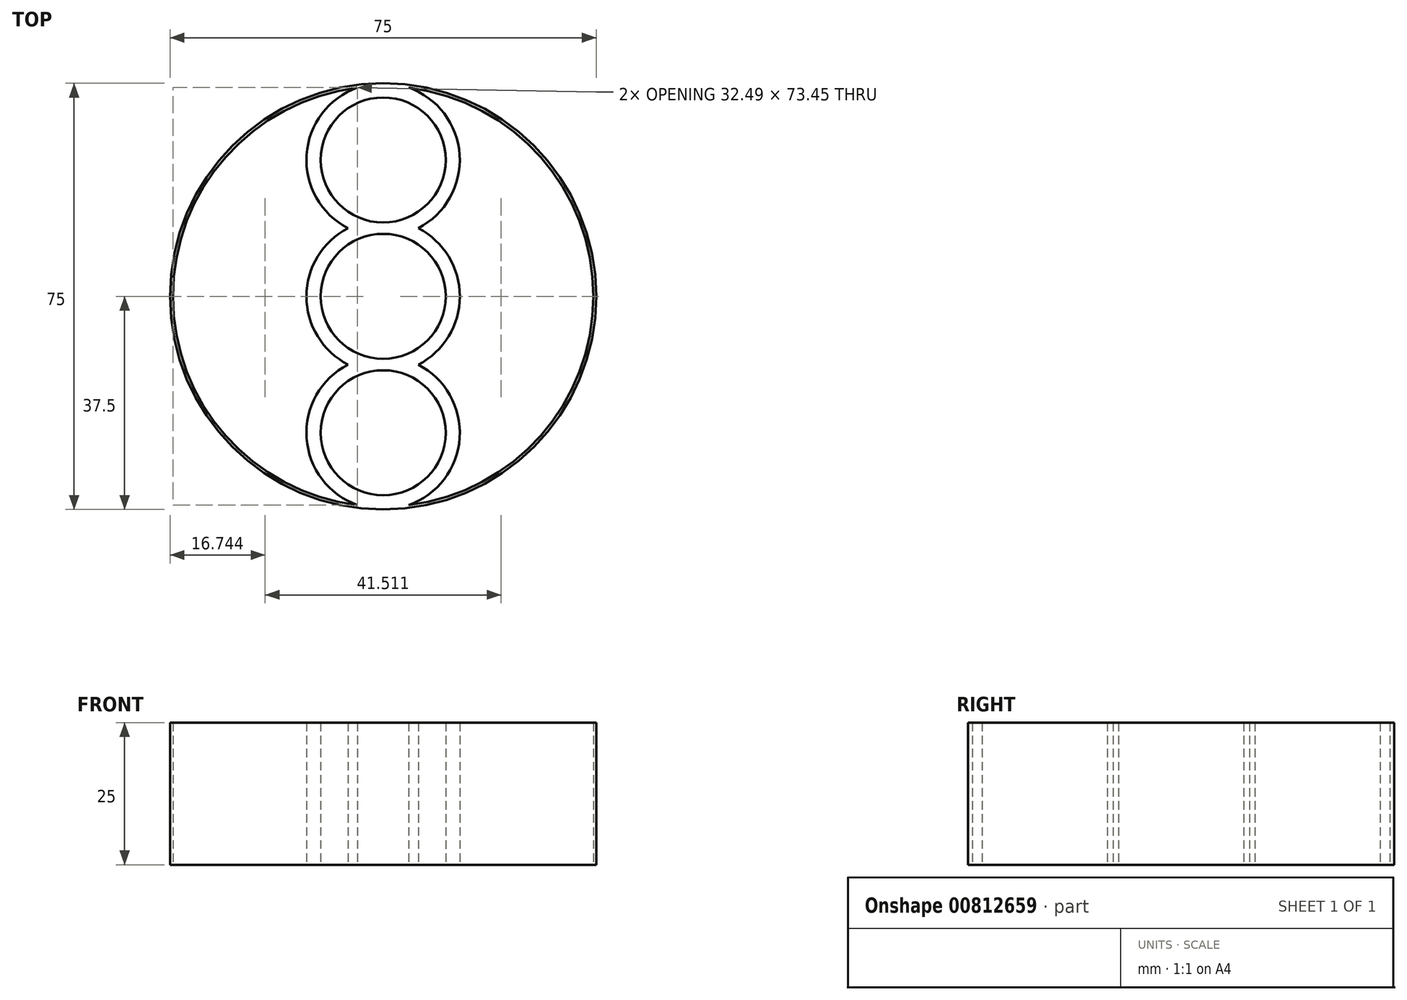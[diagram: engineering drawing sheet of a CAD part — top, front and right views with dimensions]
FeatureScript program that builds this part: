
annotation { "Feature Type Name" : "Feature", "Feature Type Description" : "" }
export const myFeature = defineFeature(function(context is Context, id is Id, definition is map)
    precondition{}
    {
        {
            var Q0;
            Q0=qCreatedBy(makeId("Top.planeOp"),FACE);
            var sketch = newSketch(context, id + "F0", { "sketchPlane" : qUnion([Q0])});
            skCircle(sketch, "E0", {"center": v(0, 0) * mm, "radius": 11 * mm});
            skArc(sketch, "E1", {"start": v(-6.18, 12) * mm, "mid": v(-13.5, 0) * mm, "end": v(-6.18, -12) * mm});
            skLineSegment(sketch, "E2", {"start": v(0, 0) * mm, "end": v(0, 13.5) * mm});
            skArc(sketch, "E3", {"start": v(6.18, 12) * mm, "mid": v(13.47, 24.91) * mm, "end": v(4.51, 36.72) * mm});
            skCircle(sketch, "E4", {"center": v(0, 24) * mm, "radius": 11 * mm});
            skLineSegment(sketch, "E5", {"start": v(0, 0) * mm, "end": v(0, -24) * mm});
            skArc(sketch, "E6", {"start": v(-6.18, -12) * mm, "mid": v(-13.47, -24.91) * mm, "end": v(-4.51, -36.72) * mm});
            skCircle(sketch, "E7", {"center": v(0, -24) * mm, "radius": 11 * mm});
            skArc(sketch, "E8", {"start": v(-4.51, 36.72) * mm, "mid": v(-37, 0) * mm, "end": v(-4.51, -36.72) * mm});
            skCircle(sketch, "E9", {"center": v(0, 0) * mm, "radius": 37.5 * mm});
            skArc(sketch, "E10.trimOffspring", {"start": v(-4.51, 36.72) * mm, "mid": v(-13.47, 24.91) * mm, "end": v(-6.18, 12) * mm});
            skArc(sketch, "E11.trimOffspring", {"start": v(6.18, -12) * mm, "mid": v(13.5, 0) * mm, "end": v(6.18, 12) * mm});
            skArc(sketch, "E12.trimOffspring", {"start": v(4.51, -36.72) * mm, "mid": v(37, 0) * mm, "end": v(4.51, 36.72) * mm});
            skArc(sketch, "E13.trimOffspring", {"start": v(4.51, -36.72) * mm, "mid": v(13.47, -24.91) * mm, "end": v(6.18, -12) * mm});
            skSolve(sketch);
        }
        {
            var Q0;
            Q0 = qSketchRegion(id + "F0", true);
            extrude(context, id + "F1", {"entities" : qUnion([Q0]), "depth" : 3 * mm, "offsetDistance" : 25 * mm});
        }
        {
            var Q0;
            Q0 = qSketchRegion(id + "F0", true);
            extrude(context, id + "F2", {"entities" : qUnion([Q0]), "operationType" : NewBodyOperationType.ADD, "depth" : 25 * mm, "offsetDistance" : 25 * mm});
        }
    });
